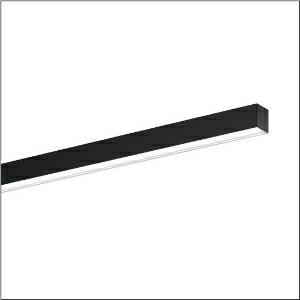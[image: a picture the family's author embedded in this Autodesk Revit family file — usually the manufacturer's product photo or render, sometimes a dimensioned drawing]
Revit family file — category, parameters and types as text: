
# Revit family: silica_r__21_51mx23db35bb_4e5d
name_source: partatom
category: Lighting Fixtures
units: mm (PartAtom-declared; Revit-internal decimal feet)

## family parameters
Cut with Voids When Loaded = No
Host = Face
Light Source = No
Part Type = Normal
Room Calculation Point = No
Round Connector Dimension = Use Diameter
Shared = No

## types (1)
- --- (1 x LED, 4100 lm, 30.1 W, 3000K)
    Apparent Load = 30 VA
    CIE Flux Codes = 78 96 99 100 100
    Color Rendering = 80
    Color Temperature = 3000K
    Default Elevation = 1800 mm
    Description = Silica® 21, office luminaire, primary optical cover: prismatic diffuser, of PMMA, CAT 2 (L<= 3000cd/m²), light emission: direct distribution, primary light characteristic: symmetric, installation type: surface-mounted, LED, rated luminous flux: 4.100lm, luminous efficacy: 136lm/W, light colour: 830, colour temperature: 3000K, control gear: DALI 2, with terminal, 3+2-pole, max. 2.5mm², mains connection: 220..240V, AC, 50/60Hz, rated input power: 30.1W, luminaire housing, of aluminium, matt jet black (RAL 9005), length: 1.504mm, width: 53mm, height: 53mm, protection rating (complete): IP20, insulation class (complete): insulation class I (protective earthing), certification: CE, permissible operating ambient temperature: 0..+35°C, standard: EN 50419, packaging unit: 1 piece
    Height = 53 mm
    Lamp = 1 x LED
    Lamp Light Flux = 4100 lm
    Lamp Power = 30.1 W
    Lamp count = 1
    Length = 1504 mm
    Luminous efficacy = 136 lm/W
    Manufacturer = Siteco
    ModVariant = No
    Model = 51MX23DB35BB
    Mounting Place = Ceiling
    Mounting Type = Surface mounted
    Number of Poles = 1
    OnlyDefault = Yes
    Power Factor = 1
    Product Name = Silica® 21
    Product group = office luminaire | ceiling mounted
    ProductGroupID = 302
    Protection Class = Protection class I
    Protection Degree = IP 20
    RLX_Detail_Level = 1
    RLX_Emergency_Light_Flux = 0 lm
    RLX_Emergency_Type = 0
    RLX_Emergency_Type_DB = No
    RlxData = <blob elided: 23805 chars, md5=1bddfbe8>
    Socket = socket
    Standby Power = 0 W
    System Light Flux = 4100 lm
    System Power = 30 W
    Type Comments = factory setting: luminous flux: 100 % | dim-lin: 254 | 345 mA
    Type Image = l_1335925.jpg
    URL = http://relux.com
    VarID = @adj_119380
    Voltage = 0 V
    Weight = 0.00 kg
    Width = 53 mm

## geometry (parser evidence)
native form markers: Blend x4, Sweep x10
no freeform markers — native parametric forms only
